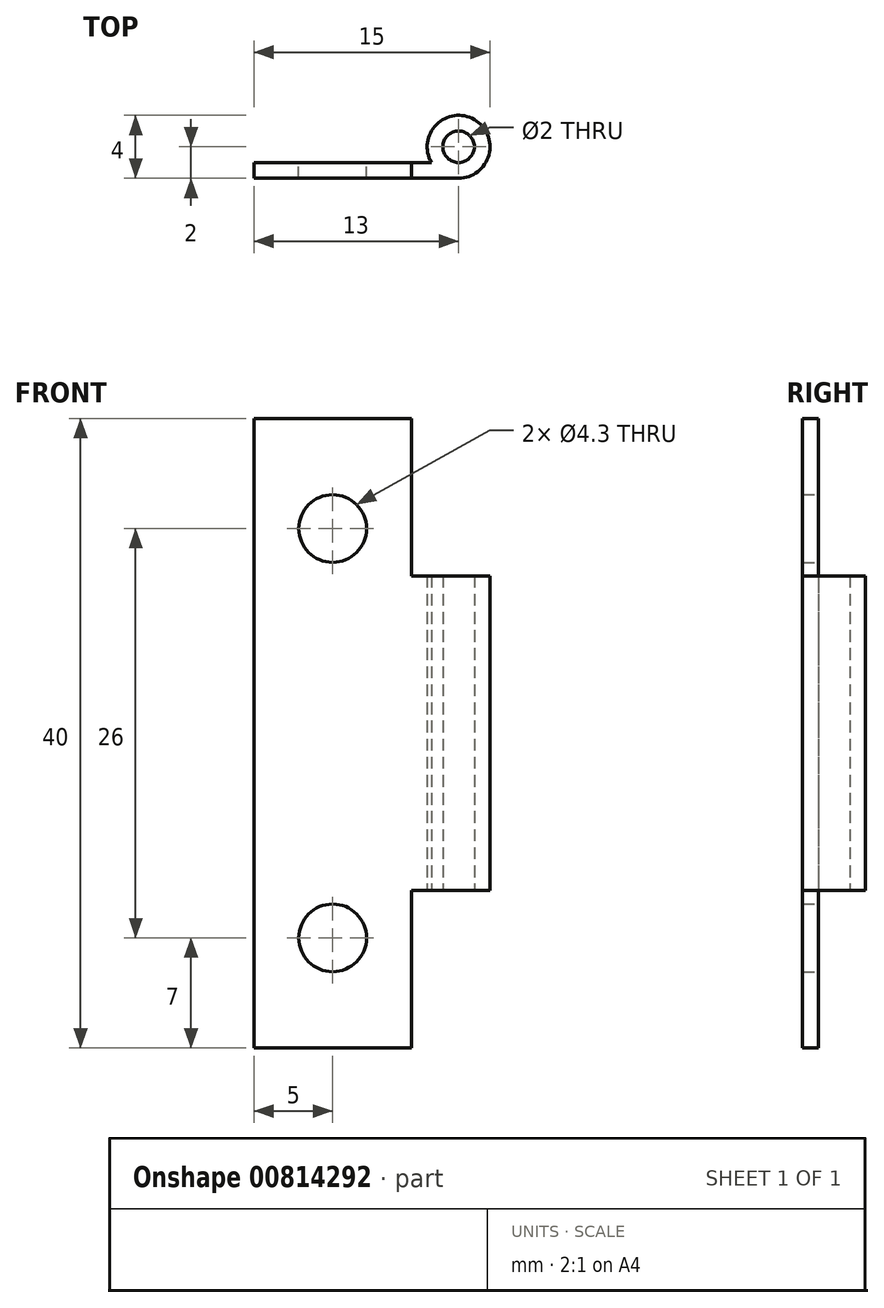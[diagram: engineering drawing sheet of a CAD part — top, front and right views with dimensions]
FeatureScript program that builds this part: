
annotation { "Feature Type Name" : "Feature", "Feature Type Description" : "" }
export const myFeature = defineFeature(function(context is Context, id is Id, definition is map)
    precondition{}
    {
        {
            var Q0;
            Q0=qCreatedBy(makeId("Front.planeOp"),FACE);
            var sketch = newSketch(context, id + "F0", { "sketchPlane" : qUnion([Q0])});
            skLineSegment(sketch, "E0.bottom", {"start": v(5, 20) * mm, "end": v(-5, 20) * mm});
            skLineSegment(sketch, "E0.top", {"start": v(5, -20) * mm, "end": v(-5, -20) * mm});
            skLineSegment(sketch, "E0.left", {"start": v(5, 20) * mm, "end": v(5, -20) * mm});
            skLineSegment(sketch, "E0.right", {"start": v(-5, 20) * mm, "end": v(-5, -20) * mm});
            skPoint(sketch, "E0.middle", {"position": v(0, 0) * mm});
            skLineSegment(sketch, "E1.left", {"start": v(5, 20) * mm, "end": v(5, 10) * mm});
            skLineSegment(sketch, "E2.left", {"start": v(5, -20) * mm, "end": v(5, -10) * mm});
            skLineSegment(sketch, "E3.bottom", {"start": v(5, -10) * mm, "end": v(8, -10) * mm});
            skLineSegment(sketch, "E3.top", {"start": v(5, 10) * mm, "end": v(8, 10) * mm});
            skLineSegment(sketch, "E3.left", {"start": v(5, 10) * mm, "end": v(5, -10) * mm});
            skLineSegment(sketch, "E3.right", {"start": v(8, 10) * mm, "end": v(8, -10) * mm});
            skSolve(sketch);
        }
        {
            var Q0;
            Q0=makeQuery(id+"F0.imprint","IMPRINT",FACE,{"disambiguationData":[TD([[makeQuery(id+"F0.imprint","IMPRINT",EDGE,{"derivedFrom":sQuery(id+"F0.wireOp",EDGE,"E0.bottom")}),1.0]])]});
            var Q1;
            Q1=makeQuery(id+"F0.imprint","IMPRINT",FACE,{"disambiguationData":[TD([[makeQuery(id+"F0.imprint","IMPRINT",EDGE,{"derivedFrom":sQuery(id+"F0.wireOp",EDGE,"E3.bottom")}),-1.0]])]});
            var Q2;
            Q2=makeQuery(id+"F0.imprint","IMPRINT",FACE,{"disambiguationData":[TD([[makeQuery(id+"F0.imprint","IMPRINT",EDGE,{"derivedFrom":sQuery(id+"F0.wireOp",EDGE,"E3.bottom")}),1.0]])]});
            extrude(context, id + "F1", {"entities" : qUnion([Q0, Q1, Q2]), "depth" : 1 * mm, "offsetDistance" : 25 * mm});
        }
        {
            var Q0;
            Q0=makeQuery(id+"F1.opExtrude","SWEPT_FACE",FACE,{"disambiguationData":[OSD([sQuery(id+"F0.wireOp",EDGE,"E3.right")])]});
            var sketch = newSketch(context, id + "F2", { "sketchPlane" : qUnion([Q0])});
            skLineSegment(sketch, "E4", {"start": v(1, -10) * mm, "end": v(1, 10) * mm, "construction": true});
            skSolve(sketch);
        }
        {
            var Q0;
            {var subQ0=sQuery(id+"F0.wireOp",EDGE,"E3.right");Q0=makeQuery(id+"F2.imprint","IMPRINT",FACE,{"disambiguationData":[TD([[makeQuery(id+"F2.imprint","IMPRINT",EDGE,{"derivedFrom":makeQuery(id+"F1.opExtrude","CAP_EDGE",EDGE,{"disambiguationData":[OSD([subQ0])],"isStart":true})}),-1.0]])]});}
            var Q1;
            Q1=makeQuery(id+"F2.imprint","IMPRINT",FACE,{"disambiguationData":[TD([[makeQuery(id+"F2.imprint","IMPRINT",EDGE,{"derivedFrom":sQuery(id+"F2.wireOp",EDGE,"4aa50bdb-2dd2-46a3-a7ca-656cc49c01c4.0.0")}),1.0]])]});
            var Q2;
            Q2=sQuery(id+"F2.wireOp",EDGE,"E4");
            revolve(context, id + "F3", {"operationType" : NewBodyOperationType.ADD, "surfaceOperationType" : NewSurfaceOperationType.NEW, "entities" : qUnion([Q0, Q1]), "axis" : qUnion([Q2]), "revolveType" : RevolveType.FULL});
        }
        {
            var Q0;
            Q0=makeQuery(id+"F1.opExtrude","CAP_FACE",FACE,{"disambiguationData":[OSD([sQuery(id+"F0.wireOp",EDGE,"E0.bottom"),sQuery(id+"F0.wireOp",EDGE,"E0.top"),sQuery(id+"F0.wireOp",EDGE,"E0.left"),sQuery(id+"F0.wireOp",EDGE,"E0.right"),sQuery(id+"F0.wireOp",EDGE,"E2.left"),sQuery(id+"F0.wireOp",EDGE,"E1.left"),sQuery(id+"F0.wireOp",EDGE,"E3.bottom"),sQuery(id+"F0.wireOp",EDGE,"E3.top"),sQuery(id+"F0.wireOp",EDGE,"E3.right")])],"isStart":false});
            var sketch = newSketch(context, id + "F4", { "sketchPlane" : qUnion([Q0])});
            skPoint(sketch, "E5", {"position": v(0, -13) * mm});
            skPoint(sketch, "E6", {"position": v(0, 13) * mm});
            skSolve(sketch);
        }
        {
            var Q0;
            Q0=sQuery(id+"F4.wireOp",VERTEX,"E6");
            var Q1;
            Q1=sQuery(id+"F4.wireOp",VERTEX,"E5");
            var Q2;
            Q2=makeQuery(id+"F1.opExtrude","SWEPT_BODY",BODY,{"disambiguationData":[OSD([sQuery(id+"F0.wireOp",EDGE,"E0.bottom"),sQuery(id+"F0.wireOp",EDGE,"E0.top"),sQuery(id+"F0.wireOp",EDGE,"E0.left"),sQuery(id+"F0.wireOp",EDGE,"E0.right"),sQuery(id+"F0.wireOp",EDGE,"E2.left"),sQuery(id+"F0.wireOp",EDGE,"E1.left"),sQuery(id+"F0.wireOp",EDGE,"E3.bottom"),sQuery(id+"F0.wireOp",EDGE,"E3.top"),sQuery(id+"F0.wireOp",EDGE,"E3.right")])]});
            hole(context, id + "F5", {"style" : HoleStyle.SIMPLE, "endStyle" : HoleEndStyle.BLIND, "holeDiameter" : 4.3 * mm, "majorDiameter" : 5 * mm, "holeDepth" : 2.5 * mm, "isTappedThrough" : true, "tappedDepth" : 12 * mm, "tapClearance" : 3, "locations" : qUnion([Q0, Q1]), "scope" : qUnion([Q2]), "startStyle" : HoleStartStyle.SKETCH});
        }
    });
